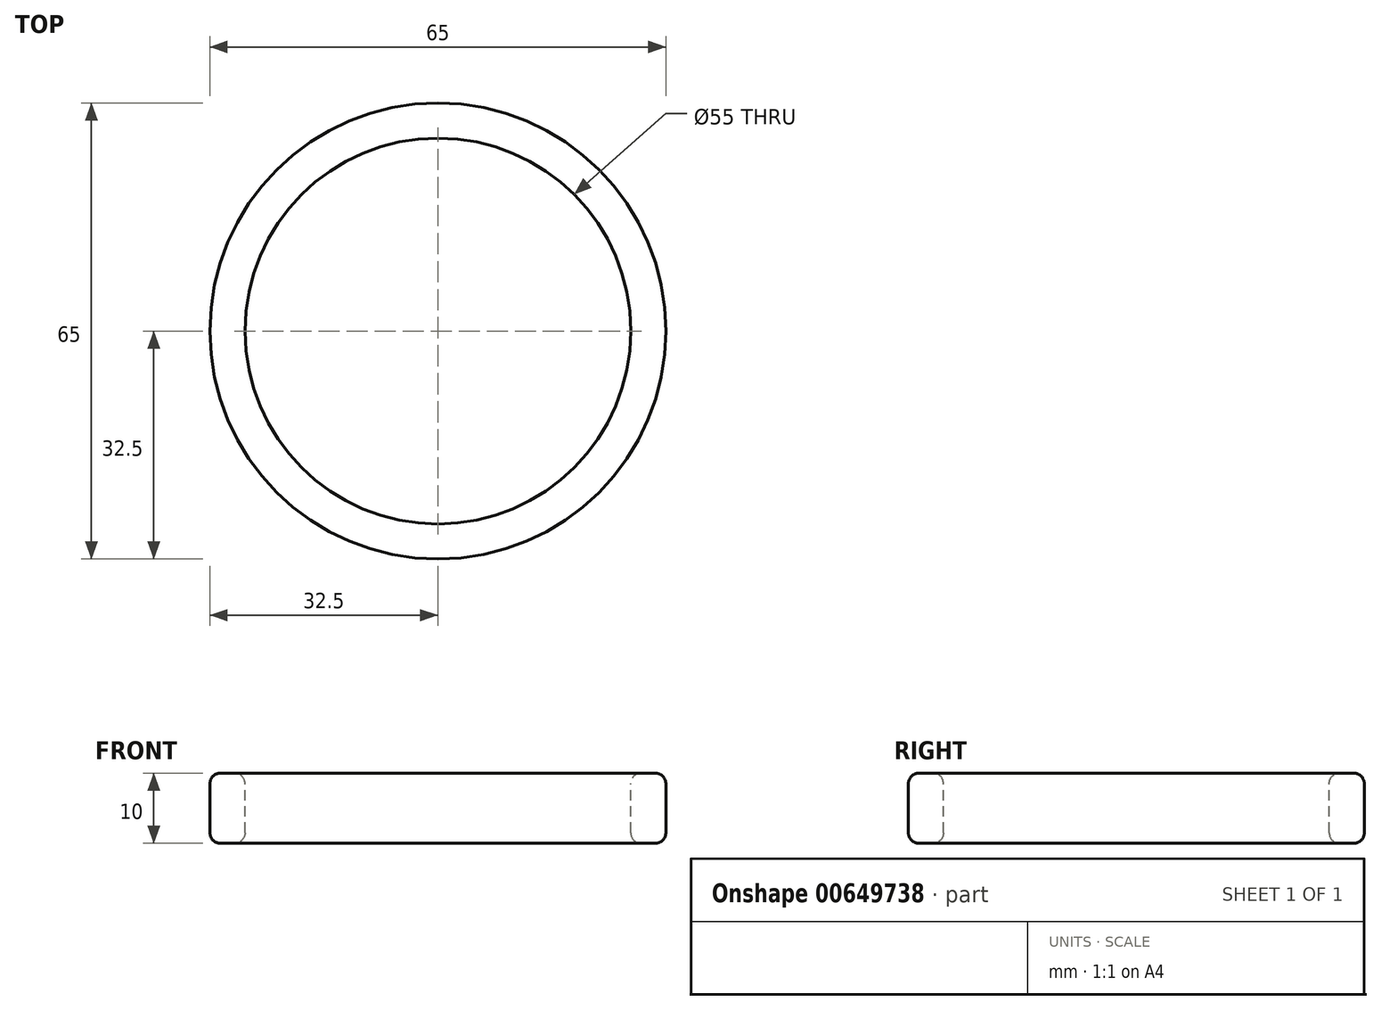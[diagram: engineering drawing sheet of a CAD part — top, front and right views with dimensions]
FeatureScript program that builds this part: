
annotation { "Feature Type Name" : "Feature", "Feature Type Description" : "" }
export const myFeature = defineFeature(function(context is Context, id is Id, definition is map)
    precondition{}
    {
        {
            var Q0;
            Q0=qCreatedBy(makeId("Front.planeOp"),FACE);
            var sketch = newSketch(context, id + "F0", { "sketchPlane" : qUnion([Q0])});
            skLineSegment(sketch, "E0.bottom", {"start": v(-31, 31.33) * mm, "end": v(-29, 31.33) * mm});
            skLineSegment(sketch, "E0.top", {"start": v(-31, 21.33) * mm, "end": v(-29, 21.33) * mm});
            skLineSegment(sketch, "E0.left", {"start": v(-32.5, 29.83) * mm, "end": v(-32.5, 22.83) * mm});
            skLineSegment(sketch, "E0.right", {"start": v(-27.5, 29.83) * mm, "end": v(-27.5, 22.83) * mm});
            skPoint(sketch, "E1.visualSharp", {"position": v(-27.5, 31.33) * mm});
            skArc(sketch, "E1.filletArc", {"start": v(-27.5, 29.83) * mm, "mid": v(-27.94, 30.89) * mm, "end": v(-29, 31.33) * mm});
            skPoint(sketch, "E2.visualSharp", {"position": v(-32.5, 31.33) * mm});
            skArc(sketch, "E2.filletArc", {"start": v(-31, 31.33) * mm, "mid": v(-32.06, 30.89) * mm, "end": v(-32.5, 29.83) * mm});
            skPoint(sketch, "E3.visualSharp", {"position": v(-32.5, 21.33) * mm});
            skArc(sketch, "E3.filletArc", {"start": v(-32.5, 22.83) * mm, "mid": v(-32.06, 21.77) * mm, "end": v(-31, 21.33) * mm});
            skPoint(sketch, "E4.visualSharp", {"position": v(-27.5, 21.33) * mm});
            skArc(sketch, "E4.filletArc", {"start": v(-29, 21.33) * mm, "mid": v(-27.94, 21.77) * mm, "end": v(-27.5, 22.83) * mm});
            skLineSegment(sketch, "E5", {"start": v(0, 42.46) * mm, "end": v(0, 0) * mm, "construction": true});
            skSolve(sketch);
        }
        {
            var Q0;
            Q0=makeQuery(id+"F0.imprint","IMPRINT",FACE,{"disambiguationData":[TD([[makeQuery(id+"F0.imprint","IMPRINT",EDGE,{"derivedFrom":sQuery(id+"F0.wireOp",EDGE,"E0.bottom")}),-1.0]])]});
            var Q1;
            Q1=sQuery(id+"F0.wireOp",EDGE,"E5");
            revolve(context, id + "F1", {"entities" : qUnion([Q0]), "axis" : qUnion([Q1]), "revolveType" : RevolveType.FULL});
        }
    });
